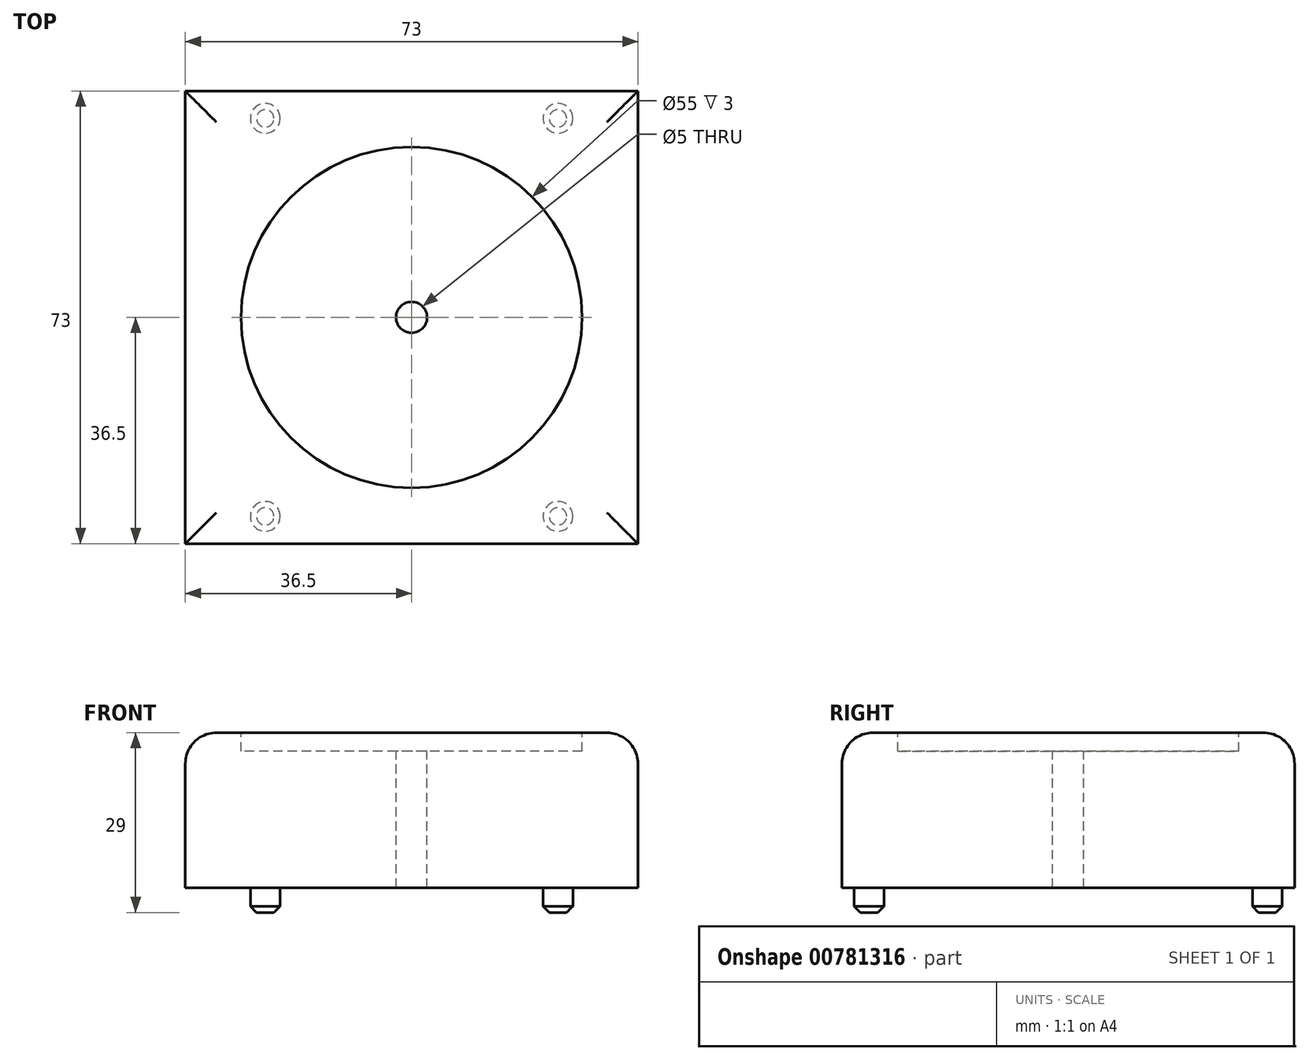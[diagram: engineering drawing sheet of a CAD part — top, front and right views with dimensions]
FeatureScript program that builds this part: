
annotation { "Feature Type Name" : "Feature", "Feature Type Description" : "" }
export const myFeature = defineFeature(function(context is Context, id is Id, definition is map)
    precondition{}
    {
        {
            var Q0;
            Q0=qCreatedBy(makeId("Top.planeOp"),FACE);
            var sketch = newSketch(context, id + "F0", { "sketchPlane" : qUnion([Q0])});
            skLineSegment(sketch, "E0.bottom", {"start": v(36.5, -36.5) * mm, "end": v(-36.5, -36.5) * mm});
            skLineSegment(sketch, "E0.top", {"start": v(36.5, 36.5) * mm, "end": v(-36.5, 36.5) * mm});
            skLineSegment(sketch, "E0.left", {"start": v(36.5, -36.5) * mm, "end": v(36.5, 36.5) * mm});
            skLineSegment(sketch, "E0.right", {"start": v(-36.5, -36.5) * mm, "end": v(-36.5, 36.5) * mm});
            skPoint(sketch, "E0.middle", {"position": v(0, 0) * mm});
            skSolve(sketch);
        }
        {
            var Q0;
            Q0 = qSketchRegion(id + "F0", true);
            extrude(context, id + "F1", {"entities" : qUnion([Q0]), "depth" : 25 * mm, "offsetDistance" : 25 * mm});
        }
        {
            var Q0;
            Q0=makeQuery(id+"F1.opExtrude","CAP_EDGE",EDGE,{"disambiguationData":[OSD([sQuery(id+"F0.wireOp",EDGE,"E0.top")])],"isStart":false});
            var Q1;
            Q1=makeQuery(id+"F1.opExtrude","CAP_FACE",FACE,{"disambiguationData":[OSD([sQuery(id+"F0.wireOp",EDGE,"E0.bottom"),sQuery(id+"F0.wireOp",EDGE,"E0.top"),sQuery(id+"F0.wireOp",EDGE,"E0.left"),sQuery(id+"F0.wireOp",EDGE,"E0.right")])],"isStart":false});
            fillet(context, id + "F2", {"entities" : qUnion([Q0, Q1]), "radius" : 5 * mm, "tangentPropagation" : true, "allowEdgeOverflow" : false});
        }
        {
            var Q0;
            Q0=makeQuery(id+"F1.opExtrude","CAP_FACE",FACE,{"disambiguationData":[OSD([sQuery(id+"F0.wireOp",EDGE,"E0.bottom"),sQuery(id+"F0.wireOp",EDGE,"E0.top"),sQuery(id+"F0.wireOp",EDGE,"E0.left"),sQuery(id+"F0.wireOp",EDGE,"E0.right")])],"isStart":false});
            var sketch = newSketch(context, id + "F3", { "sketchPlane" : qUnion([Q0])});
            skCircle(sketch, "E1", {"center": v(0, 0) * mm, "radius": 27.5 * mm});
            skSolve(sketch);
        }
        {
            var Q0;
            Q0 = qSketchRegion(id + "F3", true);
            extrude(context, id + "F4", {"entities" : qUnion([Q0]), "operationType" : NewBodyOperationType.REMOVE, "oppositeDirection" : true, "depth" : 3 * mm, "offsetDistance" : 25 * mm});
        }
        {
            var Q0;
            Q0=makeQuery(id+"F0.imprint","IMPRINT",FACE,{"disambiguationData":[TD([[makeQuery(id+"F0.imprint","IMPRINT",EDGE,{"derivedFrom":sQuery(id+"F0.wireOp",EDGE,"E0.bottom")}),-1.0]])]});
            var sketch = newSketch(context, id + "F5", { "sketchPlane" : qUnion([Q0])});
            skLineSegment(sketch, "E2.0.0", {"start": v(36.5, -36.5) * mm, "end": v(36.5, 36.5) * mm, "construction": true});
            skLineSegment(sketch, "E2.0.1", {"start": v(36.5, 36.5) * mm, "end": v(-36.5, 36.5) * mm, "construction": true});
            skLineSegment(sketch, "E2.0.2", {"start": v(-36.5, 36.5) * mm, "end": v(-36.5, -36.5) * mm, "construction": true});
            skLineSegment(sketch, "E2.0.3", {"start": v(-36.5, -36.5) * mm, "end": v(36.5, -36.5) * mm, "construction": true});
            skLineSegment(sketch, "E3.bottom", {"start": v(-23.6, -32.1) * mm, "end": v(23.6, -32.1) * mm, "construction": true});
            skLineSegment(sketch, "E3.top", {"start": v(-23.6, 32.1) * mm, "end": v(23.6, 32.1) * mm, "construction": true});
            skLineSegment(sketch, "E3.left", {"start": v(-23.6, -32.1) * mm, "end": v(-23.6, 32.1) * mm, "construction": true});
            skLineSegment(sketch, "E3.right", {"start": v(23.6, -32.1) * mm, "end": v(23.6, 32.1) * mm, "construction": true});
            skPoint(sketch, "E3.middle", {"position": v(0, 0) * mm});
            skCircle(sketch, "E4", {"center": v(-23.6, -32.1) * mm, "radius": 2.4 * mm});
            skCircle(sketch, "E5", {"center": v(23.6, -32.1) * mm, "radius": 2.4 * mm});
            skCircle(sketch, "E6", {"center": v(-23.6, 32.1) * mm, "radius": 2.4 * mm});
            skCircle(sketch, "E7", {"center": v(23.6, 32.1) * mm, "radius": 2.4 * mm});
            skSolve(sketch);
        }
        {
            var Q0;
            Q0 = qSketchRegion(id + "F5", true);
            extrude(context, id + "F6", {"entities" : qUnion([Q0]), "operationType" : NewBodyOperationType.ADD, "oppositeDirection" : true, "depth" : 4 * mm, "offsetDistance" : 25 * mm});
        }
        {
            var Q0;
            Q0=makeQuery(id+"F6.opExtrude","CAP_EDGE",EDGE,{"disambiguationData":[OSD([sQuery(id+"F5.wireOp",EDGE,"E4")])],"isStart":false});
            var Q1;
            Q1=makeQuery(id+"F6.opExtrude","CAP_EDGE",EDGE,{"disambiguationData":[OSD([sQuery(id+"F5.wireOp",EDGE,"E6")])],"isStart":false});
            var Q2;
            Q2=makeQuery(id+"F6.opExtrude","CAP_EDGE",EDGE,{"disambiguationData":[OSD([sQuery(id+"F5.wireOp",EDGE,"E7")])],"isStart":false});
            var Q3;
            Q3=makeQuery(id+"F6.opExtrude","CAP_EDGE",EDGE,{"disambiguationData":[OSD([sQuery(id+"F5.wireOp",EDGE,"E5")])],"isStart":false});
            chamfer(context, id + "F7", {"entities" : qUnion([Q0, Q1, Q2, Q3]), "width" : 1 * mm, "tangentPropagation" : true});
        }
        {
            var Q0;
            Q0=qCreatedBy(makeId("Top.planeOp"),FACE);
            cPlane(context, id + "F8", {"entities" : qUnion([Q0]), "cplaneType" : CPlaneType.OFFSET, "offset" : 40.1 * mm, "width" : 150 * mm, "height" : 150 * mm});
        }
        {
            var Q0;
            Q0=qCreatedBy(id+"F8.planeOp",FACE);
            var sketch = newSketch(context, id + "F9", { "sketchPlane" : qUnion([Q0])});
            skPoint(sketch, "E8.0", {"position": v(0, 0) * mm});
            skLineSegment(sketch, "E9.bottom", {"start": v(55.26, 49.01) * mm, "end": v(-55.26, 49.01) * mm});
            skLineSegment(sketch, "E9.top", {"start": v(55.26, -49.01) * mm, "end": v(-55.26, -49.01) * mm});
            skLineSegment(sketch, "E9.left", {"start": v(55.26, 49.01) * mm, "end": v(55.26, -49.01) * mm});
            skLineSegment(sketch, "E9.right", {"start": v(-55.26, 49.01) * mm, "end": v(-55.26, -49.01) * mm});
            skSolve(sketch);
        }
        {
            var Q0;
            Q0 = qSketchRegion(id + "F9", true);
            var Q1;
            Q1=makeQuery(id+"F1.opExtrude","CAP_FACE",FACE,{"disambiguationData":[OSD([sQuery(id+"F0.wireOp",EDGE,"E0.bottom"),sQuery(id+"F0.wireOp",EDGE,"E0.top"),sQuery(id+"F0.wireOp",EDGE,"E0.left"),sQuery(id+"F0.wireOp",EDGE,"E0.right")])],"isStart":true});
            extrude(context, id + "F10", {"entities" : qUnion([Q0]), "endBound" : BoundingType.UP_TO_SURFACE, "oppositeDirection" : true, "depth" : 59 * mm, "endBoundEntityFace" : qUnion([Q1]), "offsetDistance" : 25 * mm});
        }
        {
            var Q0;
            Q0=makeQuery(id+"F1.opExtrude","SWEPT_BODY",BODY,{"disambiguationData":[OSD([sQuery(id+"F0.wireOp",EDGE,"E0.bottom"),sQuery(id+"F0.wireOp",EDGE,"E0.top"),sQuery(id+"F0.wireOp",EDGE,"E0.left"),sQuery(id+"F0.wireOp",EDGE,"E0.right")])]});
            var Q1;
            Q1=makeQuery(id+"F10.opExtrude","SWEPT_BODY",BODY,{"disambiguationData":[OSD([sQuery(id+"F9.wireOp",EDGE,"E9.bottom"),sQuery(id+"F9.wireOp",EDGE,"E9.top"),sQuery(id+"F9.wireOp",EDGE,"E9.left"),sQuery(id+"F9.wireOp",EDGE,"E9.right")])]});
            var Q2;
            Q2=makeQuery(id+"F1.opExtrude","CAP_FACE",FACE,{"disambiguationData":[OSD([sQuery(id+"F0.wireOp",EDGE,"E0.bottom"),sQuery(id+"F0.wireOp",EDGE,"E0.top"),sQuery(id+"F0.wireOp",EDGE,"E0.left"),sQuery(id+"F0.wireOp",EDGE,"E0.right")])],"isStart":false});
            var Q3;
            Q3=makeQuery(id+"F4.boolean.opBoolean","COPY",FACE,{"derivedFrom":makeQuery(id+"F4.opExtrude","SWEPT_FACE",FACE,{"disambiguationData":[OSD([sQuery(id+"F3.wireOp",EDGE,"E1")])]})});
            var Q4;
            Q4=makeQuery(id+"F4.boolean.opBoolean","COPY",FACE,{"derivedFrom":makeQuery(id+"F4.opExtrude","CAP_FACE",FACE,{"disambiguationData":[OSD([sQuery(id+"F3.wireOp",EDGE,"E1")])],"isStart":false})});
            var Q5;
            Q5=makeQuery(id+"F6.opExtrude","SWEPT_FACE",FACE,{"disambiguationData":[OSD([sQuery(id+"F5.wireOp",EDGE,"E7")])]});
            var Q6;
            Q6=makeQuery(id+"F6.opExtrude","SWEPT_FACE",FACE,{"disambiguationData":[OSD([sQuery(id+"F5.wireOp",EDGE,"E6")])]});
            var Q7;
            Q7=makeQuery(id+"F7.opChamfer","BLEND_FACE",FACE,{"disambiguationData":[OSD([sQuery(id+"F5.wireOp",EDGE,"E6")])]});
            var Q8;
            Q8=makeQuery(id+"F1.opExtrude","CAP_FACE",FACE,{"disambiguationData":[OSD([sQuery(id+"F0.wireOp",EDGE,"E0.bottom"),sQuery(id+"F0.wireOp",EDGE,"E0.top"),sQuery(id+"F0.wireOp",EDGE,"E0.left"),sQuery(id+"F0.wireOp",EDGE,"E0.right")])],"isStart":true});
            var Q9;
            Q9=makeQuery(id+"F1.opExtrude","SWEPT_FACE",FACE,{"disambiguationData":[OSD([sQuery(id+"F0.wireOp",EDGE,"E0.right")])]});
            var Q10;
            Q10=makeQuery(id+"F1.opExtrude","SWEPT_FACE",FACE,{"disambiguationData":[OSD([sQuery(id+"F0.wireOp",EDGE,"E0.top")])]});
            var Q11;
            Q11=makeQuery(id+"F2.opFillet","BLEND_FACE",FACE,{"disambiguationData":[OSD([sQuery(id+"F0.wireOp",EDGE,"E0.bottom")])]});
            var Q12;
            Q12=makeQuery(id+"F2.opFillet","BLEND_FACE",FACE,{"disambiguationData":[OSD([sQuery(id+"F0.wireOp",EDGE,"E0.left")])]});
            var Q13;
            Q13=makeQuery(id+"F1.opExtrude","SWEPT_FACE",FACE,{"disambiguationData":[OSD([sQuery(id+"F0.wireOp",EDGE,"E0.bottom")])]});
            var Q14;
            Q14=makeQuery(id+"F2.opFillet","BLEND_FACE",FACE,{"disambiguationData":[OSD([sQuery(id+"F0.wireOp",EDGE,"E0.top")])]});
            var Q15;
            Q15=makeQuery(id+"F2.opFillet","BLEND_FACE",FACE,{"disambiguationData":[OSD([sQuery(id+"F0.wireOp",EDGE,"E0.right")])]});
            var Q16;
            Q16=makeQuery(id+"F7.opChamfer","BLEND_FACE",FACE,{"disambiguationData":[OSD([sQuery(id+"F5.wireOp",EDGE,"E7")])]});
            var Q17;
            Q17=makeQuery(id+"F6.opExtrude","CAP_FACE",FACE,{"disambiguationData":[OSD([sQuery(id+"F5.wireOp",EDGE,"E7")])],"isStart":false});
            var Q18;
            Q18=makeQuery(id+"F6.opExtrude","SWEPT_FACE",FACE,{"disambiguationData":[OSD([sQuery(id+"F5.wireOp",EDGE,"E4")])]});
            var Q19;
            Q19=makeQuery(id+"F1.opExtrude","SWEPT_FACE",FACE,{"disambiguationData":[OSD([sQuery(id+"F0.wireOp",EDGE,"E0.left")])]});
            var Q20;
            Q20=makeQuery(id+"F6.opExtrude","SWEPT_FACE",FACE,{"disambiguationData":[OSD([sQuery(id+"F5.wireOp",EDGE,"E5")])]});
            var Q21;
            Q21=makeQuery(id+"F6.opExtrude","CAP_FACE",FACE,{"disambiguationData":[OSD([sQuery(id+"F5.wireOp",EDGE,"E6")])],"isStart":false});
            var Q22;
            Q22=makeQuery(id+"F7.opChamfer","BLEND_FACE",FACE,{"disambiguationData":[OSD([sQuery(id+"F5.wireOp",EDGE,"E5")])]});
            var Q23;
            Q23=makeQuery(id+"F7.opChamfer","BLEND_FACE",FACE,{"disambiguationData":[OSD([sQuery(id+"F5.wireOp",EDGE,"E4")])]});
            var Q24;
            Q24=makeQuery(id+"F6.opExtrude","CAP_FACE",FACE,{"disambiguationData":[OSD([sQuery(id+"F5.wireOp",EDGE,"E5")])],"isStart":false});
            var Q25;
            Q25=makeQuery(id+"F6.opExtrude","CAP_FACE",FACE,{"disambiguationData":[OSD([sQuery(id+"F5.wireOp",EDGE,"E4")])],"isStart":false});
            booleanBodies(context, id + "F11", {"operationType" : BooleanOperationType.SUBTRACTION, "tools" : qUnion([Q0]), "targets" : qUnion([Q1]), "offset" : true, "entitiesToOffset" : qUnion([Q2, Q3, Q4, Q5, Q6, Q7, Q8, Q9, Q10, Q11, Q12, Q13, Q14, Q15, Q16, Q17, Q18, Q19, Q20, Q21, Q22, Q23, Q24, Q25]), "offsetDistance" : .5 * mm, "keepTools" : true});
        }
        {
            var Q0;
            Q0=makeQuery(id+"F10.opExtrude","SWEPT_BODY",BODY,{"disambiguationData":[OSD([sQuery(id+"F9.wireOp",EDGE,"E9.bottom"),sQuery(id+"F9.wireOp",EDGE,"E9.top"),sQuery(id+"F9.wireOp",EDGE,"E9.left"),sQuery(id+"F9.wireOp",EDGE,"E9.right")])]});
            deleteBodies(context, id + "F12", {"entities" : qUnion([Q0])});
        }
        {
            var Q0;
            Q0=makeQuery(id+"F4.boolean.opBoolean","COPY",FACE,{"derivedFrom":makeQuery(id+"F4.opExtrude","CAP_FACE",FACE,{"disambiguationData":[OSD([sQuery(id+"F3.wireOp",EDGE,"E1")])],"isStart":false})});
            var sketch = newSketch(context, id + "F13", { "sketchPlane" : qUnion([Q0])});
            skPoint(sketch, "E10.0", {"position": v(0, 0) * mm});
            skSolve(sketch);
        }
        {
            var Q0;
            Q0=sQuery(id+"F13.wireOp",VERTEX,"E10.0");
            var Q1;
            Q1=makeQuery(id+"F1.opExtrude","SWEPT_BODY",BODY,{"disambiguationData":[OSD([sQuery(id+"F0.wireOp",EDGE,"E0.bottom"),sQuery(id+"F0.wireOp",EDGE,"E0.top"),sQuery(id+"F0.wireOp",EDGE,"E0.left"),sQuery(id+"F0.wireOp",EDGE,"E0.right")])]});
            hole(context, id + "F14", {"style" : HoleStyle.SIMPLE, "endStyle" : HoleEndStyle.THROUGH, "holeDiameter" : 5 * mm, "majorDiameter" : 5 * mm, "isTappedThrough" : true, "tappedDepth" : 12 * mm, "tapClearance" : 3, "locations" : qUnion([Q0]), "scope" : qUnion([Q1])});
        }
    });
